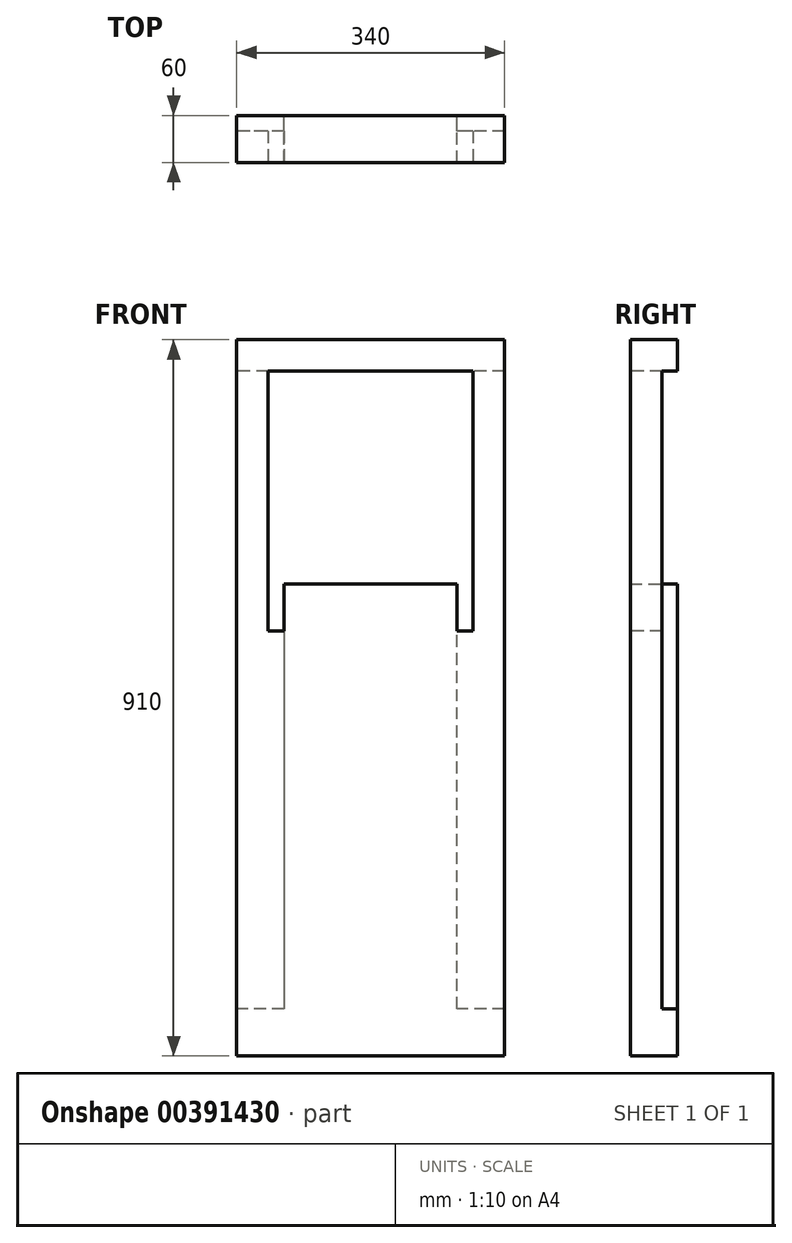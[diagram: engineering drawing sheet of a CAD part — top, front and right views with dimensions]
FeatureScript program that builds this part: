
annotation { "Feature Type Name" : "Feature", "Feature Type Description" : "" }
export const myFeature = defineFeature(function(context is Context, id is Id, definition is map)
    precondition{}
    {
        {
            var Q0;
            Q0=qCreatedBy(makeId("Front.planeOp"),FACE);
            var sketch = newSketch(context, id + "F0", { "sketchPlane" : qUnion([Q0])});
            skLineSegment(sketch, "E0.bottom", {"start": v(170, 455) * mm, "end": v(-170, 455) * mm});
            skLineSegment(sketch, "E0.top", {"start": v(170, -455) * mm, "end": v(-170, -455) * mm});
            skLineSegment(sketch, "E0.left", {"start": v(170, 455) * mm, "end": v(170, -455) * mm});
            skLineSegment(sketch, "E0.right", {"start": v(-170, 455) * mm, "end": v(-170, -455) * mm});
            skPoint(sketch, "E0.middle", {"position": v(0, 0) * mm});
            skLineSegment(sketch, "E1", {"start": v(170, -455) * mm, "end": v(170, -395) * mm});
            skLineSegment(sketch, "E2", {"start": v(170, -395) * mm, "end": v(-170, -395) * mm});
            skLineSegment(sketch, "E3", {"start": v(-170, -395) * mm, "end": v(-110, -395) * mm});
            skLineSegment(sketch, "E4", {"start": v(-110, -395) * mm, "end": v(-110, 95) * mm});
            skLineSegment(sketch, "E5", {"start": v(170, -395) * mm, "end": v(110, -395) * mm});
            skLineSegment(sketch, "E6", {"start": v(110, -395) * mm, "end": v(110, 95) * mm});
            skLineSegment(sketch, "E7", {"start": v(110, 95) * mm, "end": v(-110, 95) * mm});
            skLineSegment(sketch, "E8", {"start": v(110, 95) * mm, "end": v(110, 145) * mm});
            skLineSegment(sketch, "E9", {"start": v(110, 145) * mm, "end": v(-110, 145) * mm});
            skLineSegment(sketch, "E10", {"start": v(-110, 145) * mm, "end": v(-110, 95) * mm});
            skLineSegment(sketch, "E11", {"start": v(110, 145) * mm, "end": v(130, 145) * mm});
            skLineSegment(sketch, "E12", {"start": v(170, 455) * mm, "end": v(130, 455) * mm});
            skLineSegment(sketch, "E13", {"start": v(130, 455) * mm, "end": v(130, 145) * mm});
            skLineSegment(sketch, "E14", {"start": v(170, 455) * mm, "end": v(170, 415) * mm});
            skLineSegment(sketch, "E15", {"start": v(170, 415) * mm, "end": v(-170, 415) * mm});
            skLineSegment(sketch, "E16", {"start": v(-170, 455) * mm, "end": v(-130, 455) * mm});
            skLineSegment(sketch, "E17", {"start": v(-130, 455) * mm, "end": v(-130, 145) * mm});
            skLineSegment(sketch, "E18", {"start": v(-130, 145) * mm, "end": v(-110, 145) * mm});
            skSolve(sketch);
        }
        {
            var Q0;
            Q0=makeQuery(id+"F0.imprint","IMPRINT",FACE,{"disambiguationData":[TD([[makeQuery(id+"F0.imprint","IMPRINT",EDGE,{"derivedFrom":sQuery(id+"F0.wireOp",EDGE,"E0.bottom")}),1.0]])]});
            var Q1;
            {var subQ0=sQuery(id+"F0.wireOp",EDGE,"E12");Q1=makeQuery(id+"F0.imprint","IMPRINT",FACE,{"disambiguationData":[TD([[makeQuery(id+"F0.imprint","IMPRINT",EDGE,{"derivedFrom":subQ0}),1.0]])]});}
            var Q2;
            {var subQ0=sQuery(id+"F0.wireOp",EDGE,"E16");Q2=makeQuery(id+"F0.imprint","IMPRINT",FACE,{"disambiguationData":[TD([[makeQuery(id+"F0.imprint","IMPRINT",EDGE,{"derivedFrom":subQ0}),-1.0]])]});}
            var Q3;
            {var subQ0=sQuery(id+"F0.wireOp",EDGE,"E3");Q3=makeQuery(id+"F0.imprint","IMPRINT",FACE,{"disambiguationData":[TD([[makeQuery(id+"F0.imprint","IMPRINT",EDGE,{"derivedFrom":subQ0}),1.0]])]});}
            var Q4;
            {var subQ0=sQuery(id+"F0.wireOp",EDGE,"E0.left");Q4=makeQuery(id+"F0.imprint","IMPRINT",FACE,{"disambiguationData":[TD([[makeQuery(id+"F0.imprint","IMPRINT",EDGE,{"derivedFrom":subQ0}),-1.0]])]});}
            var Q5;
            Q5=makeQuery(id+"F0.imprint","IMPRINT",FACE,{"disambiguationData":[TD([[makeQuery(id+"F0.imprint","IMPRINT",EDGE,{"derivedFrom":sQuery(id+"F0.wireOp",EDGE,"E7")}),-1.0]])]});
            var Q6;
            {var subQ1=sQuery(id+"F0.wireOp",EDGE,"E0.top");Q6=makeQuery(id+"F0.imprint","IMPRINT",FACE,{"disambiguationData":[TD([[makeQuery(id+"F0.imprint","IMPRINT",EDGE,{"derivedFrom":subQ1}),-1.0]])]});}
            var Q7;
            Q7=makeQuery(id+"F0.imprint","IMPRINT",FACE,{"disambiguationData":[TD([[makeQuery(id+"F0.imprint","IMPRINT",EDGE,{"derivedFrom":sQuery(id+"F0.wireOp",EDGE,"E2")}),-1.0]])]});
            extrude(context, id + "F1", {"entities" : qUnion([Q0, Q1, Q2, Q3, Q4, Q5, Q6, Q7]), "depth" : 60 * mm});
        }
        {
            var Q0;
            Q0=makeQuery(id+"F1.opExtrude","CAP_FACE",FACE,{"disambiguationData":[OSD([sQuery(id+"F0.wireOp",EDGE,"E0.bottom"),sQuery(id+"F0.wireOp",EDGE,"E0.top"),sQuery(id+"F0.wireOp",EDGE,"E0.left"),sQuery(id+"F0.wireOp",EDGE,"E0.right"),sQuery(id+"F0.wireOp",EDGE,"E1"),sQuery(id+"F0.wireOp",EDGE,"E9"),sQuery(id+"F0.wireOp",EDGE,"E11"),sQuery(id+"F0.wireOp",EDGE,"E12"),sQuery(id+"F0.wireOp",EDGE,"E13"),sQuery(id+"F0.wireOp",EDGE,"E14"),sQuery(id+"F0.wireOp",EDGE,"E15"),sQuery(id+"F0.wireOp",EDGE,"E16"),sQuery(id+"F0.wireOp",EDGE,"E17"),sQuery(id+"F0.wireOp",EDGE,"E18")])],"isStart":false});
            var sketch = newSketch(context, id + "F2", { "sketchPlane" : qUnion([Q0])});
            skLineSegment(sketch, "E19.bottom", {"start": v(-130, 415) * mm, "end": v(130, 415) * mm});
            skLineSegment(sketch, "E19.top", {"start": v(-130, 145) * mm, "end": v(130, 145) * mm});
            skLineSegment(sketch, "E19.left", {"start": v(-130, 415) * mm, "end": v(-130, 145) * mm});
            skLineSegment(sketch, "E19.right", {"start": v(130, 415) * mm, "end": v(130, 145) * mm});
            skLineSegment(sketch, "E20", {"start": v(170, -455) * mm, "end": v(-170, -455) * mm});
            skLineSegment(sketch, "E21", {"start": v(-170, -455) * mm, "end": v(-170, 455) * mm});
            skLineSegment(sketch, "E22", {"start": v(-170, 455) * mm, "end": v(170, 455) * mm});
            skLineSegment(sketch, "E23", {"start": v(170, 455) * mm, "end": v(170, -455) * mm});
            skLineSegment(sketch, "E24", {"start": v(-130, 145) * mm, "end": v(-130, 85) * mm});
            skLineSegment(sketch, "E25", {"start": v(130, 145) * mm, "end": v(130, 85) * mm});
            skLineSegment(sketch, "E26", {"start": v(130, 85) * mm, "end": v(-130, 85) * mm});
            skLineSegment(sketch, "E27", {"start": v(-130, 115) * mm, "end": v(-170, 115) * mm});
            skLineSegment(sketch, "E28", {"start": v(130, 115) * mm, "end": v(170, 115) * mm});
            skSolve(sketch);
        }
        {
            var Q0;
            Q0 = qSketchRegion(id + "F2", true);
            extrude(context, id + "F3", {"entities" : qUnion([Q0]), "operationType" : NewBodyOperationType.ADD, "oppositeDirection" : true, "depth" : 40 * mm});
        }
    });
